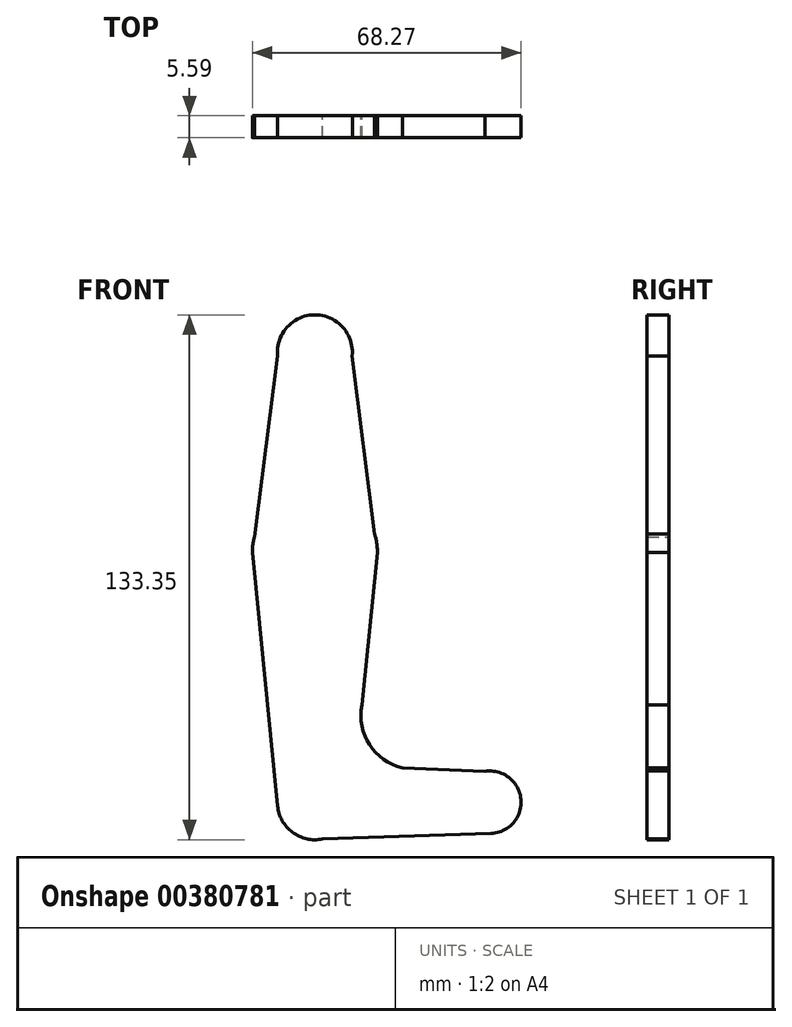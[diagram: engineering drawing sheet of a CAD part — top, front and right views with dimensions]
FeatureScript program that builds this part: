
annotation { "Feature Type Name" : "Feature", "Feature Type Description" : "" }
export const myFeature = defineFeature(function(context is Context, id is Id, definition is map)
    precondition{}
    {
        {
            var Q0;
            Q0=qCreatedBy(makeId("Front.planeOp"),FACE);
            var sketch = newSketch(context, id + "F0", { "sketchPlane" : qUnion([Q0])});
            skCircle(sketch, "E0", {"center": v(0, 50.8) * mm, "radius": 9.53 * mm});
            skCircle(sketch, "E1", {"center": v(0, 0) * mm, "radius": 15.88 * mm});
            skCircle(sketch, "E2", {"center": v(0, -63.5) * mm, "radius": 9.53 * mm});
            skCircle(sketch, "E3", {"center": v(44.45, -63.5) * mm, "radius": 7.94 * mm});
            skLineSegment(sketch, "E4", {"start": v(-15.39, 3.9) * mm, "end": v(-9.48, 49.9) * mm});
            skLineSegment(sketch, "E5", {"start": v(-15.88, 0) * mm, "end": v(-9.48, -64.4) * mm});
            skLineSegment(sketch, "E6", {"start": v(15.16, 4.7) * mm, "end": v(9.48, 49.9) * mm});
            skCircle(sketch, "E7", {"center": v(-4.31, 36.53) * mm, "radius": 1.59 * mm});
            skArc(sketch, "E8", {"start": v(11.9, -38.84) * mm, "mid": v(13.88, -48.87) * mm, "end": v(22.23, -54.77) * mm});
            skLineSegment(sketch, "E9", {"start": v(15.88, 0) * mm, "end": v(11.9, -38.84) * mm});
            skLineSegment(sketch, "E10", {"start": v(22.23, -54.77) * mm, "end": v(43.2, -55.66) * mm});
            skLineSegment(sketch, "E11", {"start": v(1.9, -72.83) * mm, "end": v(44.7, -71.43) * mm});
            skCircle(sketch, "E12", {"center": v(0, 50.8) * mm, "radius": 3.18 * mm});
            skCircle(sketch, "E13", {"center": v(0, -0.02) * mm, "radius": 3.18 * mm});
            skCircle(sketch, "E14", {"center": v(-0.27, -63.84) * mm, "radius": 3.18 * mm});
            skCircle(sketch, "E15", {"center": v(44.35, -64.1) * mm, "radius": 3.18 * mm});
            skSolve(sketch);
        }
        {
            var Q0;
            {var subQ10=sQuery(id+"F0.wireOp",EDGE,"E8");Q0=makeQuery(id+"F0.imprint","IMPRINT",FACE,{"disambiguationData":[TD([[makeQuery(id+"F0.imprint","IMPRINT",EDGE,{"derivedFrom":subQ10}),-1.0]])]});}
            var Q1;
            Q1=makeQuery(id+"F0.imprint","IMPRINT",FACE,{"disambiguationData":[TD([[makeQuery(id+"F0.imprint","IMPRINT",EDGE,{"derivedFrom":sQuery(id+"F0.wireOp",EDGE,"E13")}),-1.0]])]});
            var Q2;
            {var subQ0=sQuery(id+"F0.wireOp",EDGE,"E4");Q2=makeQuery(id+"F0.imprint","IMPRINT",FACE,{"disambiguationData":[TD([[makeQuery(id+"F0.imprint","IMPRINT",EDGE,{"derivedFrom":subQ0}),-1.0]])]});}
            var Q3;
            Q3=makeQuery(id+"F0.imprint","IMPRINT",FACE,{"disambiguationData":[TD([[makeQuery(id+"F0.imprint","IMPRINT",EDGE,{"derivedFrom":sQuery(id+"F0.wireOp",EDGE,"E15")}),-1.0]])]});
            var Q4;
            Q4=makeQuery(id+"F0.imprint","IMPRINT",FACE,{"disambiguationData":[TD([[makeQuery(id+"F0.imprint","IMPRINT",EDGE,{"derivedFrom":sQuery(id+"F0.wireOp",EDGE,"E14")}),-1.0]])]});
            var Q5;
            Q5=makeQuery(id+"F0.imprint","IMPRINT",FACE,{"disambiguationData":[TD([[makeQuery(id+"F0.imprint","IMPRINT",EDGE,{"derivedFrom":sQuery(id+"F0.wireOp",EDGE,"E14")}),1.0]])]});
            var Q6;
            Q6=makeQuery(id+"F0.imprint","IMPRINT",FACE,{"disambiguationData":[TD([[makeQuery(id+"F0.imprint","IMPRINT",EDGE,{"derivedFrom":sQuery(id+"F0.wireOp",EDGE,"E12")}),1.0]])]});
            var Q7;
            Q7=makeQuery(id+"F0.imprint","IMPRINT",FACE,{"disambiguationData":[TD([[makeQuery(id+"F0.imprint","IMPRINT",EDGE,{"derivedFrom":sQuery(id+"F0.wireOp",EDGE,"E12")}),-1.0]])]});
            var Q8;
            {var subQ0=sQuery(id+"F0.wireOp",EDGE,"E5");var subQ1=sQuery(id+"F0.wireOp",EDGE,"E1");var subQ2=makeQuery(id+"F0.imprint","INTERSECT",VERTEX,{"disambiguationData":[OD(0.0)],"derivedFrom":[subQ1,subQ0]});Q8=makeQuery(id+"F0.imprint","IMPRINT",FACE,{"disambiguationData":[TD([[makeQuery(id+"F0.imprint","IMPRINT",EDGE,{"disambiguationData":[TD([[subQ2,-1.0]])],"derivedFrom":subQ1}),1.0]])]});}
            var Q9;
            {var subQ0=sQuery(id+"F0.wireOp",EDGE,"E9");var subQ1=sQuery(id+"F0.wireOp",EDGE,"E1");var subQ2=makeQuery(id+"F0.imprint","INTERSECT",VERTEX,{"disambiguationData":[OD(0.0)],"derivedFrom":[subQ1,subQ0]});Q9=makeQuery(id+"F0.imprint","IMPRINT",FACE,{"disambiguationData":[TD([[makeQuery(id+"F0.imprint","IMPRINT",EDGE,{"disambiguationData":[TD([[subQ2,1.0]])],"derivedFrom":subQ1}),1.0]])]});}
            var Q10;
            Q10=makeQuery(id+"F0.imprint","IMPRINT",FACE,{"disambiguationData":[TD([[makeQuery(id+"F0.imprint","IMPRINT",EDGE,{"derivedFrom":sQuery(id+"F0.wireOp",EDGE,"E7")}),1.0]])]});
            var Q11;
            Q11=makeQuery(id+"F0.imprint","IMPRINT",FACE,{"disambiguationData":[TD([[makeQuery(id+"F0.imprint","IMPRINT",EDGE,{"derivedFrom":sQuery(id+"F0.wireOp",EDGE,"E13")}),1.0]])]});
            var Q12;
            Q12=makeQuery(id+"F0.imprint","IMPRINT",FACE,{"disambiguationData":[TD([[makeQuery(id+"F0.imprint","IMPRINT",EDGE,{"derivedFrom":sQuery(id+"F0.wireOp",EDGE,"E15")}),1.0]])]});
            extrude(context, id + "F1", {"entities" : qUnion([Q0, Q1, Q2, Q3, Q4, Q5, Q6, Q7, Q8, Q9, Q10, Q11, Q12]), "depth" : 5.6 * mm});
        }
    });
